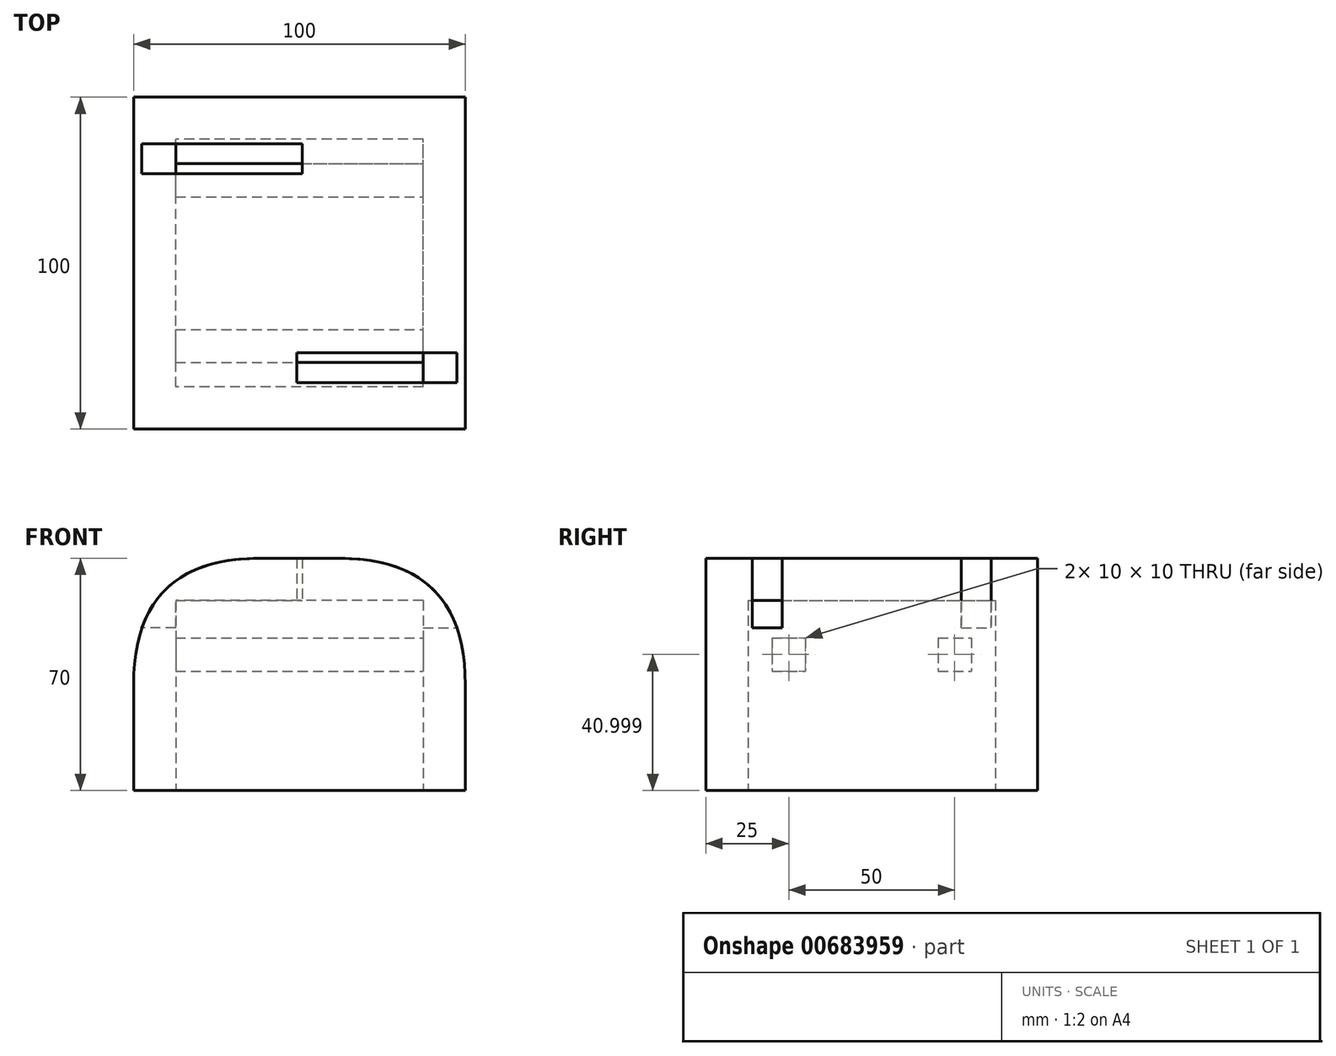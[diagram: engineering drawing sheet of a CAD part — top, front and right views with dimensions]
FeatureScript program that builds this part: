
annotation { "Feature Type Name" : "Feature", "Feature Type Description" : "" }
export const myFeature = defineFeature(function(context is Context, id is Id, definition is map)
    precondition{}
    {
        {
            var Q0;
            Q0=qCreatedBy(makeId("Front.planeOp"),FACE);
            var sketch = newSketch(context, id + "F0", { "sketchPlane" : qUnion([Q0])});
            skLineSegment(sketch, "E0.bottom", {"start": v(34.09, -17.92) * mm, "end": v(-65.91, -17.92) * mm});
            skLineSegment(sketch, "E0.top", {"start": v(34.09, -87.92) * mm, "end": v(-65.91, -87.92) * mm});
            skLineSegment(sketch, "E0.left", {"start": v(34.09, -17.92) * mm, "end": v(34.09, -87.92) * mm});
            skLineSegment(sketch, "E0.right", {"start": v(-65.91, -17.92) * mm, "end": v(-65.91, -87.92) * mm});
            skSolve(sketch);
        }
        {
            var Q0;
            Q0=makeQuery(id+"F0.imprint","IMPRINT",FACE,{"disambiguationData":[TD([[makeQuery(id+"F0.imprint","IMPRINT",EDGE,{"derivedFrom":sQuery(id+"F0.wireOp",EDGE,"E0.bottom")}),1.0]])]});
            extrude(context, id + "F1", {"entities" : qUnion([Q0]), "depth" : 100 * mm, "offsetDistance" : 25.4 * mm});
        }
        {
            var Q0;
            Q0=makeQuery(id+"F1.opExtrude","SWEPT_FACE",FACE,{"disambiguationData":[OSD([sQuery(id+"F0.wireOp",EDGE,"E0.top")])]});
            shell(context, id + "F2", {"entities" : qUnion([Q0]), "thickness" : 12.7 * mm});
        }
        {
            var Q0;
            Q0=makeQuery(id+"F1.opExtrude","SWEPT_EDGE",EDGE,{"disambiguationData":[OSD([sQuery(id+"F0.wireOp",EDGE,"E0.bottom"),sQuery(id+"F0.wireOp",EDGE,"E0.left")])]});
            fillet(context, id + "F3", {"entities" : qUnion([Q0]), "radius" : 38.1 * mm, "tangentPropagation" : true, "rho" : 0.5, "crossSection" : FilletCrossSection.CONIC, "allowEdgeOverflow" : false});
        }
        {
            var Q0;
            Q0=makeQuery(id+"F1.opExtrude","SWEPT_EDGE",EDGE,{"disambiguationData":[OSD([sQuery(id+"F0.wireOp",EDGE,"E0.bottom"),sQuery(id+"F0.wireOp",EDGE,"E0.right")])]});
            fillet(context, id + "F4", {"entities" : qUnion([Q0]), "radius" : 38.1 * mm, "tangentPropagation" : true, "rho" : 0.5, "crossSection" : FilletCrossSection.CONIC, "allowEdgeOverflow" : false});
        }
        {
            var Q0;
            Q0=makeQuery(id+"F1.opExtrude","SWEPT_FACE",FACE,{"disambiguationData":[OSD([sQuery(id+"F0.wireOp",EDGE,"E0.right")])]});
            var sketch = newSketch(context, id + "F5", { "sketchPlane" : qUnion([Q0])});
            skLineSegment(sketch, "E1.bottom", {"start": v(14, -6.92) * mm, "end": v(23, -6.92) * mm});
            skLineSegment(sketch, "E1.top", {"start": v(14, -38.92) * mm, "end": v(23, -38.92) * mm});
            skLineSegment(sketch, "E1.left", {"start": v(14, -6.92) * mm, "end": v(14, -38.92) * mm});
            skLineSegment(sketch, "E1.right", {"start": v(23, -6.92) * mm, "end": v(23, -38.92) * mm});
            skSolve(sketch);
        }
        {
            var Q0;
            Q0=qSketchRegion(id+"F5",true);
            extrude(context, id + "F6", {"entities" : qUnion([Q0]), "operationType" : NewBodyOperationType.REMOVE, "oppositeDirection" : true, "depth" : 50.8 * mm, "offsetDistance" : 25.4 * mm});
        }
        {
            var Q0;
            Q0=makeQuery(id+"F1.opExtrude","SWEPT_FACE",FACE,{"disambiguationData":[OSD([sQuery(id+"F0.wireOp",EDGE,"E0.left")])]});
            var sketch = newSketch(context, id + "F7", { "sketchPlane" : qUnion([Q0])});
            skLineSegment(sketch, "E2.bottom", {"start": v(-86, -8.92) * mm, "end": v(-77, -8.92) * mm});
            skLineSegment(sketch, "E2.top", {"start": v(-86, -38.92) * mm, "end": v(-77, -38.92) * mm});
            skLineSegment(sketch, "E2.left", {"start": v(-86, -8.92) * mm, "end": v(-86, -38.92) * mm});
            skLineSegment(sketch, "E2.right", {"start": v(-77, -8.92) * mm, "end": v(-77, -38.92) * mm});
            skSolve(sketch);
        }
        {
            var Q0;
            Q0=qSketchRegion(id+"F7",true);
            extrude(context, id + "F8", {"entities" : qUnion([Q0]), "operationType" : NewBodyOperationType.REMOVE, "oppositeDirection" : true, "depth" : 50.8 * mm, "offsetDistance" : 25.4 * mm});
        }
        {
            var Q0;
            Q0=makeQuery(id+"F2.opShell","OFFSET_FACE",FACE,{"disambiguationData":[OSD([sQuery(id+"F0.wireOp",EDGE,"E0.left")])]});
            var sketch = newSketch(context, id + "F9", { "sketchPlane" : qUnion([Q0])});
            skLineSegment(sketch, "E3.left", {"start": v(20, -41.92) * mm, "end": v(20, -51.92) * mm});
            skLineSegment(sketch, "E3.right", {"start": v(80, -41.92) * mm, "end": v(80, -51.92) * mm});
            skLineSegment(sketch, "E4", {"start": v(70, -41.92) * mm, "end": v(70, -51.92) * mm});
            skLineSegment(sketch, "E5", {"start": v(30, -41.92) * mm, "end": v(30, -51.92) * mm});
            skLineSegment(sketch, "E6", {"start": v(80, -41.92) * mm, "end": v(70, -41.92) * mm});
            skLineSegment(sketch, "E7", {"start": v(80, -51.92) * mm, "end": v(70, -51.92) * mm});
            skLineSegment(sketch, "E8", {"start": v(30, -41.92) * mm, "end": v(20, -41.92) * mm});
            skLineSegment(sketch, "E9", {"start": v(30, -51.92) * mm, "end": v(20, -51.92) * mm});
            skSolve(sketch);
        }
        {
            var Q0;
            Q0=qSketchRegion(id+"F9",true);
            extrude(context, id + "F10", {"entities" : qUnion([Q0]), "operationType" : NewBodyOperationType.ADD, "depth" : 83.82 * mm, "offsetDistance" : 25.4 * mm});
        }
    });
